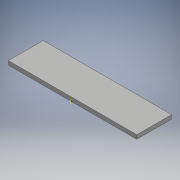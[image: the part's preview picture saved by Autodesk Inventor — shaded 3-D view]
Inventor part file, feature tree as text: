
AUTODESK INVENTOR PART (.ipt)
format: ipt  version: 2018 (Build 220112000, 112)  size: 128,000 bytes
history: native  units: mm
features: other x6, plane x1, sheet_metal_op x1, sketch x1, reference x1
ambient origin geometry x8: Origin, YZ Plane, XZ Plane, XY Plane, X Axis, Y Axis, Z Axis, Center Point
bodies: Solid1 (feature_tree)
feature tree (10):
  plane  "Work Plane1"
  sheet_metal_op  "Face1"
  other  "midtplan"
  sketch  "Sketch1"  dims[d7=3.0mm d8=12.0mm d9=12.0mm d10=26.0mm]
  reference  "Reference1"
  other  "Plate1"
  parser-record x1  (decoder bookkeeping rows leaked as tree rows — omitted from the tree; the rows remain in map.json)
  other  "modul.iam"
  other  "plade:1"
  other  "Definition1"
note: 1 file-system path scrubbed to <path> (originals preserved in map.json)
